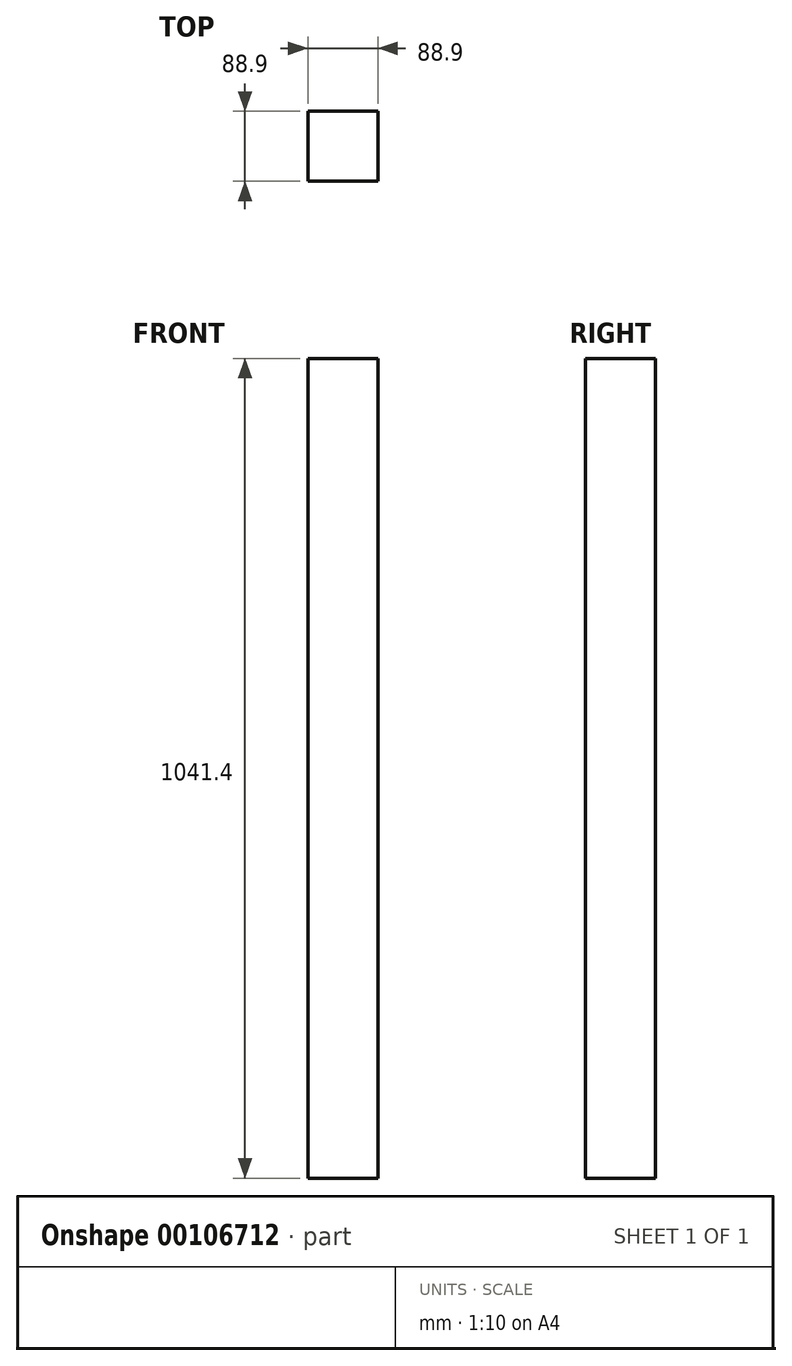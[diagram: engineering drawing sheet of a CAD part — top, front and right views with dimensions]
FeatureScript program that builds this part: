
annotation { "Feature Type Name" : "Feature", "Feature Type Description" : "" }
export const myFeature = defineFeature(function(context is Context, id is Id, definition is map)
    precondition{}
    {
        {
            var Q0;
            Q0=qCreatedBy(makeId("Top.planeOp"),FACE);
            var sketch = newSketch(context, id + "F0", { "sketchPlane" : qUnion([Q0])});
            skLineSegment(sketch, "E0.bottom", {"start": v(0, 0) * mm, "end": v(88.9, 0) * mm});
            skLineSegment(sketch, "E0.top", {"start": v(0, 88.9) * mm, "end": v(88.9, 88.9) * mm});
            skLineSegment(sketch, "E0.left", {"start": v(0, 0) * mm, "end": v(0, 88.9) * mm});
            skLineSegment(sketch, "E0.right", {"start": v(88.9, 0) * mm, "end": v(88.9, 88.9) * mm});
            skSolve(sketch);
        }
        {
            var Q0;
            Q0=makeQuery(id+"F0.imprint","IMPRINT",FACE,{"disambiguationData":[TD([[makeQuery(id+"F0.imprint","IMPRINT",EDGE,{"derivedFrom":sQuery(id+"F0.wireOp",EDGE,"E0.bottom")}),1.0]])]});
            extrude(context, id + "F1", {"entities" : qUnion([Q0]), "depth" : 1041.4 * mm});
        }
    });
